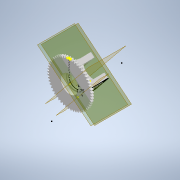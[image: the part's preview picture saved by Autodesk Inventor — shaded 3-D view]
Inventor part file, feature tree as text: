
AUTODESK INVENTOR PART (.ipt)
format: ipt  version: 2022 (Build 260153070, 153G)  size: 670,720 bytes
history: native  units: mm
features: sketch x11, extrude x11, plane x5, mirror x3, loft x2, pattern_circular x1, fillet x1, projected_geometry x1
ambient origin geometry x8: Origin, YZ Plane, XZ Plane, XY Plane, X Axis, Y Axis, Z Axis, Center Point
bodies: Solid1 (feature_tree)
feature tree (35):
  sketch  "Sketch1"  dims[d0=3.0mm d1=0.0mm]
  extrude  "Extrusion1"  TaperAngle=0.0deg  [1 undecoded]
  extrude  "Extrusion2"  Depth=540.0mm TaperAngle=360.0deg
  pattern_circular  "Circular Pattern1"  Count=2  [1 undecoded]
  sketch  "Sketch2"  dims[d2=10.0mm d3=0.0mm d4=540.0mm d5=360.0deg]
  sketch  "Sketch3"  dims[d7=22.5mm]
  extrude  "Extrusion3"  Depth=6.0mm TaperAngle=0.0deg
  sketch  "Sketch4"  dims[d8=3.0mm]
  extrude  "Extrusion4"  Depth=9.5mm TaperAngle=0.0deg
  plane  "Work Plane1"
  extrude  "Extrusion6"  Depth=4.0mm
  plane  "Work Plane2"
  fillet  "Fillet1"  Radius=5.0mm
  loft  "Loft1"
  mirror  "Mirror1"
  plane  "Work Plane6"
  sketch  "Sketch13"  dims[d14=7.5mm d15=0.0mm]
  extrude  "Extrusion7"  TaperAngle=0.0deg  [1 undecoded]
  sketch  "Sketch14"  dims[d16=3.0mm]
  loft  "Loft2"
  sketch  "Sketch15"  dims[d17=1.5mm]
  extrude  "Extrusion12"  TaperAngle=0.0deg  [1 undecoded]
  extrude  "Extrusion9"  Depth=12.5mm TaperAngle=0.0deg
  plane  "Work Plane7"
  mirror  "Mirror2"
  extrude  "Extrusion5"  Depth=2.0mm TaperAngle=0.0deg
  extrude  "Extrusion11"  Depth=24.5mm TaperAngle=0.0deg
  extrude  "Extrusion13"  Depth=25.0mm
  mirror  "Mirror3"
  sketch  "Sketch5"  dims[d9=8.5mm d10=0.0mm]
  sketch  "Sketch7"  dims[d11=1.75mm]
  sketch  "Sketch8"  dims[d12=1.5mm d13=0.0mm]
  projected_geometry  "Projected Loop1"
  plane  "Work Plane8"
  sketch  "Sketch17"  dims[d18=12.0mm d19=20.0mm d20=6.0mm d21=0.0mm d22=9.5mm d23=0.0mm d24=4.0mm d26=5.0mm d27=0.0mm d28=90.0deg d29=0.0mm d30=90.0deg d32=0.0mm d33=90.0deg d34=0.0mm d35=90.0deg d38=12.5mm d39=0.0mm d40=2.0mm d41=0.0mm d44=24.5mm d45=0.0mm d47=25.0mm d48=11.37mm d49=14.0mm d50=2.0mm d51=7.0mm d52=0.0mm d54=1.0mm d55=0.0mm d42=0.5mm d43=0.872665mm]
note: 4 required parameter values undecoded (feature->parameter linkage not recoverable at this tier; creation-order binding heuristic only, values carry confidence <= 0.55)
